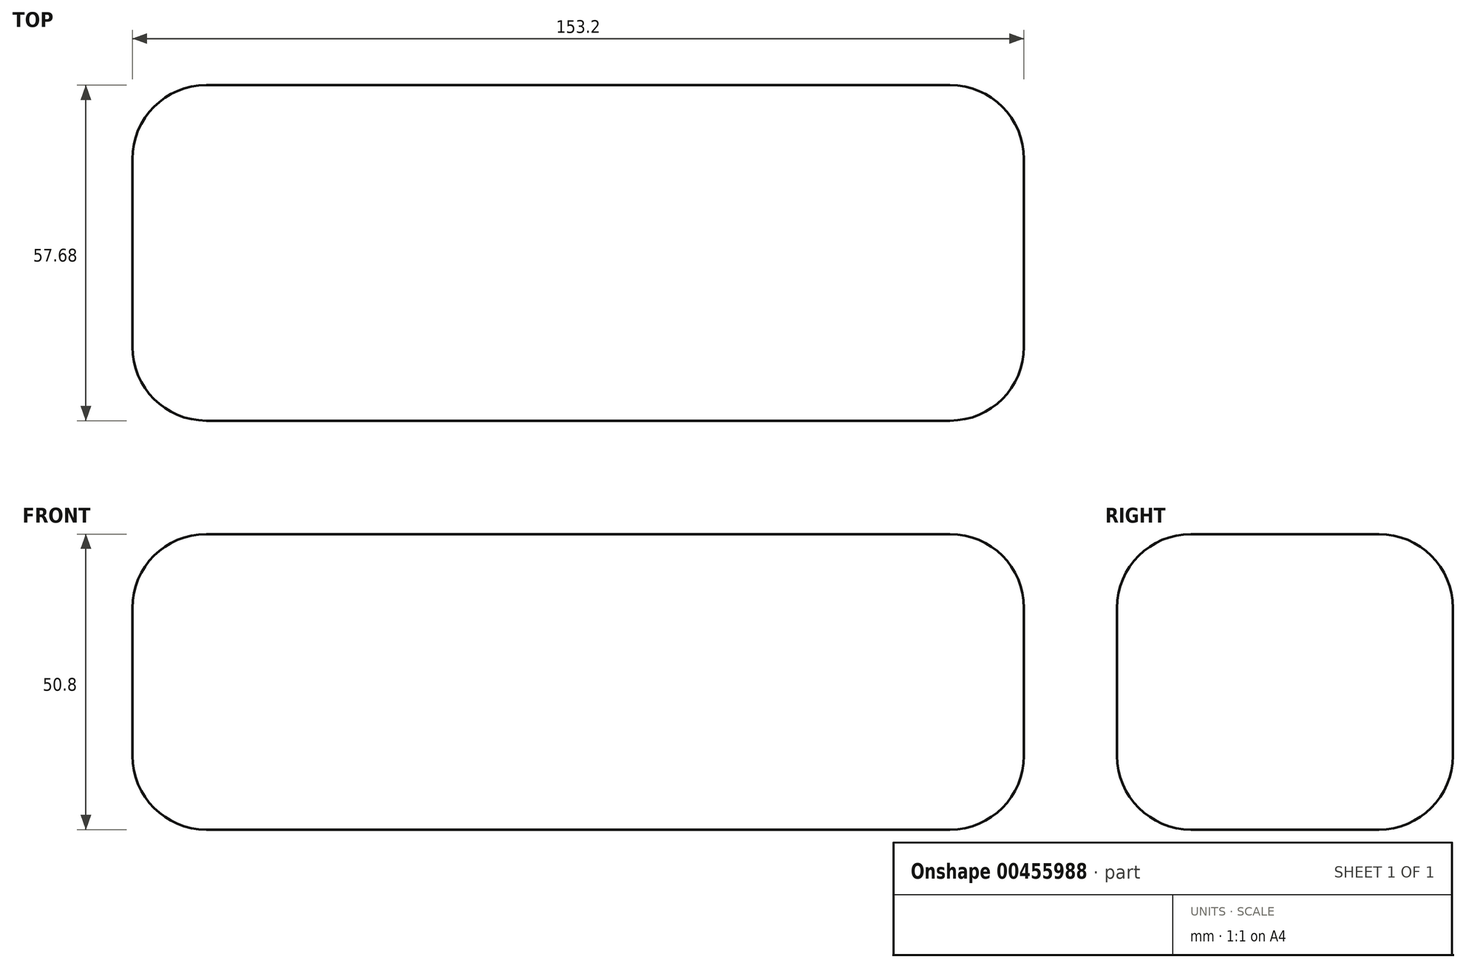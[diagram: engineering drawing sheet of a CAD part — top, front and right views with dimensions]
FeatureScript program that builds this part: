
annotation { "Feature Type Name" : "Feature", "Feature Type Description" : "" }
export const myFeature = defineFeature(function(context is Context, id is Id, definition is map)
    precondition{}
    {
        {
            var Q0;
            Q0=qCreatedBy(makeId("Top.planeOp"),FACE);
            var sketch = newSketch(context, id + "F0", { "sketchPlane" : qUnion([Q0])});
            skLineSegment(sketch, "E0.bottom", {"start": v(76.6, 28.84) * mm, "end": v(-76.6, 28.84) * mm});
            skLineSegment(sketch, "E0.top", {"start": v(76.6, -28.84) * mm, "end": v(-76.6, -28.84) * mm});
            skLineSegment(sketch, "E0.left", {"start": v(76.6, 28.84) * mm, "end": v(76.6, -28.84) * mm});
            skLineSegment(sketch, "E0.right", {"start": v(-76.6, 28.84) * mm, "end": v(-76.6, -28.84) * mm});
            skPoint(sketch, "E0.middle", {"position": v(0, 0) * mm});
            skSolve(sketch);
        }
        {
            var Q0;
            Q0=makeQuery(id+"F0.imprint","IMPRINT",FACE,{"disambiguationData":[TD([[makeQuery(id+"F0.imprint","IMPRINT",EDGE,{"derivedFrom":sQuery(id+"F0.wireOp",EDGE,"E0.bottom")}),1.0]])]});
            extrude(context, id + "F1", {"entities" : qUnion([Q0]), "depth" : 50.8 * mm});
        }
        {
            var Q0;
            Q0=makeQuery(id+"F1.opExtrude","CAP_EDGE",EDGE,{"disambiguationData":[OSD([sQuery(id+"F0.wireOp",EDGE,"E0.top")])],"isStart":false});
            var Q1;
            Q1=makeQuery(id+"F1.opExtrude","SWEPT_FACE",FACE,{"disambiguationData":[OSD([sQuery(id+"F0.wireOp",EDGE,"E0.top")])]});
            var Q2;
            Q2=makeQuery(id+"F1.opExtrude","CAP_EDGE",EDGE,{"disambiguationData":[OSD([sQuery(id+"F0.wireOp",EDGE,"E0.left")])],"isStart":false});
            var Q3;
            Q3=makeQuery(id+"F1.opExtrude","CAP_EDGE",EDGE,{"disambiguationData":[OSD([sQuery(id+"F0.wireOp",EDGE,"E0.top")])],"isStart":true});
            var Q4;
            Q4=makeQuery(id+"F1.opExtrude","SWEPT_EDGE",EDGE,{"disambiguationData":[OSD([sQuery(id+"F0.wireOp",EDGE,"E0.top"),sQuery(id+"F0.wireOp",EDGE,"E0.right")])]});
            var Q5;
            Q5=makeQuery(id+"F1.opExtrude","CAP_EDGE",EDGE,{"disambiguationData":[OSD([sQuery(id+"F0.wireOp",EDGE,"E0.right")])],"isStart":true});
            var Q6;
            Q6=makeQuery(id+"F1.opExtrude","CAP_FACE",FACE,{"disambiguationData":[OSD([sQuery(id+"F0.wireOp",EDGE,"E0.bottom"),sQuery(id+"F0.wireOp",EDGE,"E0.top"),sQuery(id+"F0.wireOp",EDGE,"E0.left"),sQuery(id+"F0.wireOp",EDGE,"E0.right")])],"isStart":true});
            var Q7;
            Q7=makeQuery(id+"F1.opExtrude","SWEPT_FACE",FACE,{"disambiguationData":[OSD([sQuery(id+"F0.wireOp",EDGE,"E0.right")])]});
            var Q8;
            Q8=makeQuery(id+"F1.opExtrude","SWEPT_FACE",FACE,{"disambiguationData":[OSD([sQuery(id+"F0.wireOp",EDGE,"E0.left")])]});
            var Q9;
            Q9=makeQuery(id+"F1.opExtrude","CAP_FACE",FACE,{"disambiguationData":[OSD([sQuery(id+"F0.wireOp",EDGE,"E0.bottom"),sQuery(id+"F0.wireOp",EDGE,"E0.top"),sQuery(id+"F0.wireOp",EDGE,"E0.left"),sQuery(id+"F0.wireOp",EDGE,"E0.right")])],"isStart":false});
            fillet(context, id + "F2", {"entities" : qUnion([Q0, Q1, Q2, Q3, Q4, Q5, Q6, Q7, Q8, Q9]), "radius" : 12.7 * mm, "tangentPropagation" : true, "allowEdgeOverflow" : false});
        }
    });
